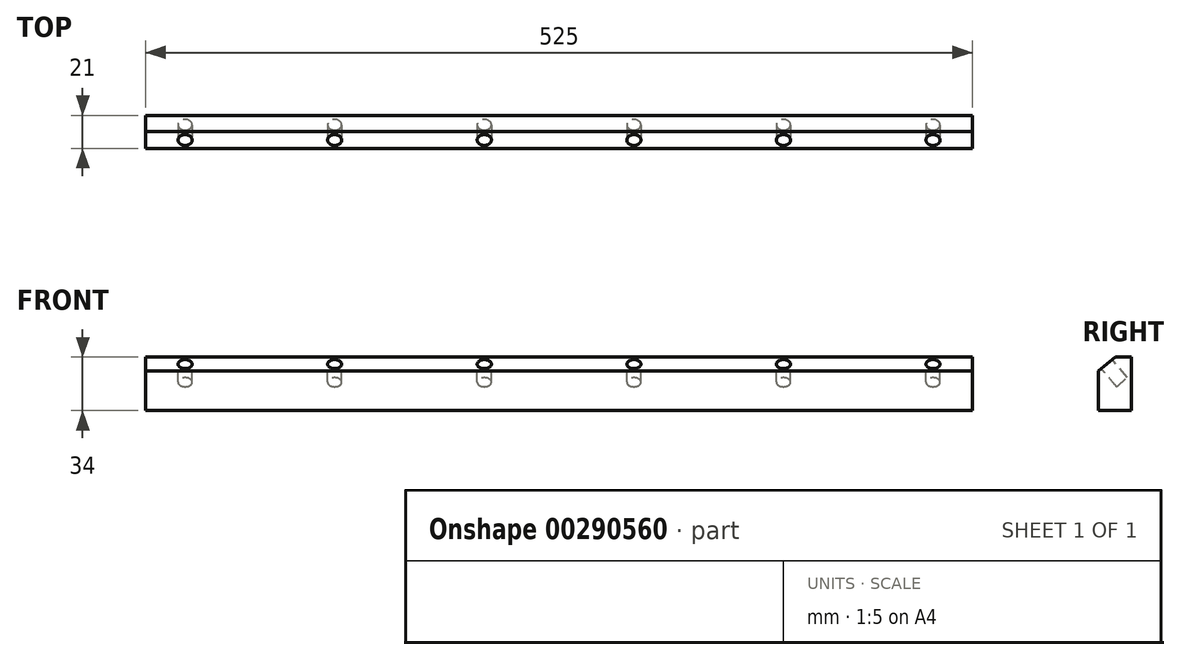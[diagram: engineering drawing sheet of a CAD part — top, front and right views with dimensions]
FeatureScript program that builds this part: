
annotation { "Feature Type Name" : "Feature", "Feature Type Description" : "" }
export const myFeature = defineFeature(function(context is Context, id is Id, definition is map)
    precondition{}
    {
        {
            var Q0;
            Q0=qCreatedBy(makeId("Right.planeOp"),FACE);
            var sketch = newSketch(context, id + "F0", { "sketchPlane" : qUnion([Q0])});
            skLineSegment(sketch, "E0", {"start": v(0, 0) * mm, "end": v(-21, 0) * mm});
            skLineSegment(sketch, "E1", {"start": v(-21, 0) * mm, "end": v(-21, 25) * mm});
            skLineSegment(sketch, "E2", {"start": v(-21, 25) * mm, "end": v(-10.27, 34) * mm});
            skLineSegment(sketch, "E3", {"start": v(-10.27, 34) * mm, "end": v(0, 34) * mm});
            skLineSegment(sketch, "E4", {"start": v(0, 34) * mm, "end": v(0, 0) * mm});
            skSolve(sketch);
        }
        {
            var Q0;
            Q0 = qSketchRegion(id + "F0", true);
            extrude(context, id + "F1", {"entities" : qUnion([Q0]), "depth" : 525 * mm});
        }
        {
            var Q0;
            Q0=makeQuery(id+"F1.opExtrude","SWEPT_FACE",FACE,{"disambiguationData":[OSD([sQuery(id+"F0.wireOp",EDGE,"E2")])]});
            var sketch = newSketch(context, id + "F2", { "sketchPlane" : qUnion([Q0])});
            skCircle(sketch, "E5", {"center": v(500, 6.98) * mm, "radius": 4.5 * mm});
            skPoint(sketch, "E5.centerSnap0", {"position": v(525, 6.98) * mm});
            skCircle(sketch, "E6.1.0.0", {"center": v(405, 6.98) * mm, "radius": 4.5 * mm});
            skCircle(sketch, "E6.2.0.0", {"center": v(310, 6.98) * mm, "radius": 4.5 * mm});
            skCircle(sketch, "E6.3.0.0", {"center": v(215, 6.98) * mm, "radius": 4.5 * mm});
            skCircle(sketch, "E6.4.0.0", {"center": v(120, 6.98) * mm, "radius": 4.5 * mm});
            skCircle(sketch, "E6.5.0.0", {"center": v(25, 6.98) * mm, "radius": 4.5 * mm});
            skLineSegment(sketch, "E6.direction1", {"start": v(500, 6.98) * mm, "end": v(405, 6.98) * mm, "construction": true});
            skSolve(sketch);
        }
        {
            var Q0;
            Q0 = qSketchRegion(id + "F2", true);
            extrude(context, id + "F3", {"entities" : qUnion([Q0]), "operationType" : NewBodyOperationType.REMOVE, "oppositeDirection" : true, "depth" : 15 * mm});
        }
    });
